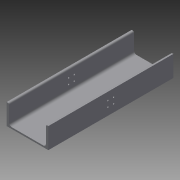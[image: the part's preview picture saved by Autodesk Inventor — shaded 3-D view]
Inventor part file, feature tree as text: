
AUTODESK INVENTOR PART (.ipt)
format: ipt  version: 2015 (Build 190159000, 159)  size: 116,736 bytes
history: native  units: in
note: dims shown in document units (in); Inventor stores cm internally (conversion verified against a paired STEP export)
features: sketch x2, extrude x1, hole x1
ambient origin geometry x8: Origin, YZ Plane, XZ Plane, XY Plane, X Axis, Y Axis, Z Axis, Center Point
bodies: Solid1 (feature_tree)
feature tree (4):
  extrude  "Extrusion1"  Depth=2.0in
  hole  "Hole2"  [1 undecoded]
  sketch  "Sketch1"  dims[d0=2.0in d1=2.0in]
  sketch  "Sketch3"  dims[d2=0.23in d3=1.85in d4=2.0in d5=0.23in d6=1.85in d7=2.0in d8=0.25in d9=0.25in d10=12.0in d11=0.0in d12=0.125in d13=0.125in d22=0.77in d23=0.144in d24=0.144in d25=0.144in d26=0.144in d31=0.15in d32=0.75in d33=0.279in d34=0.138in d35=0.5635in d36=1.0in d37=0.8108in]
note: 1 required parameter value undecoded (feature->parameter linkage not recoverable at this tier; creation-order binding heuristic only, values carry confidence <= 0.55)
